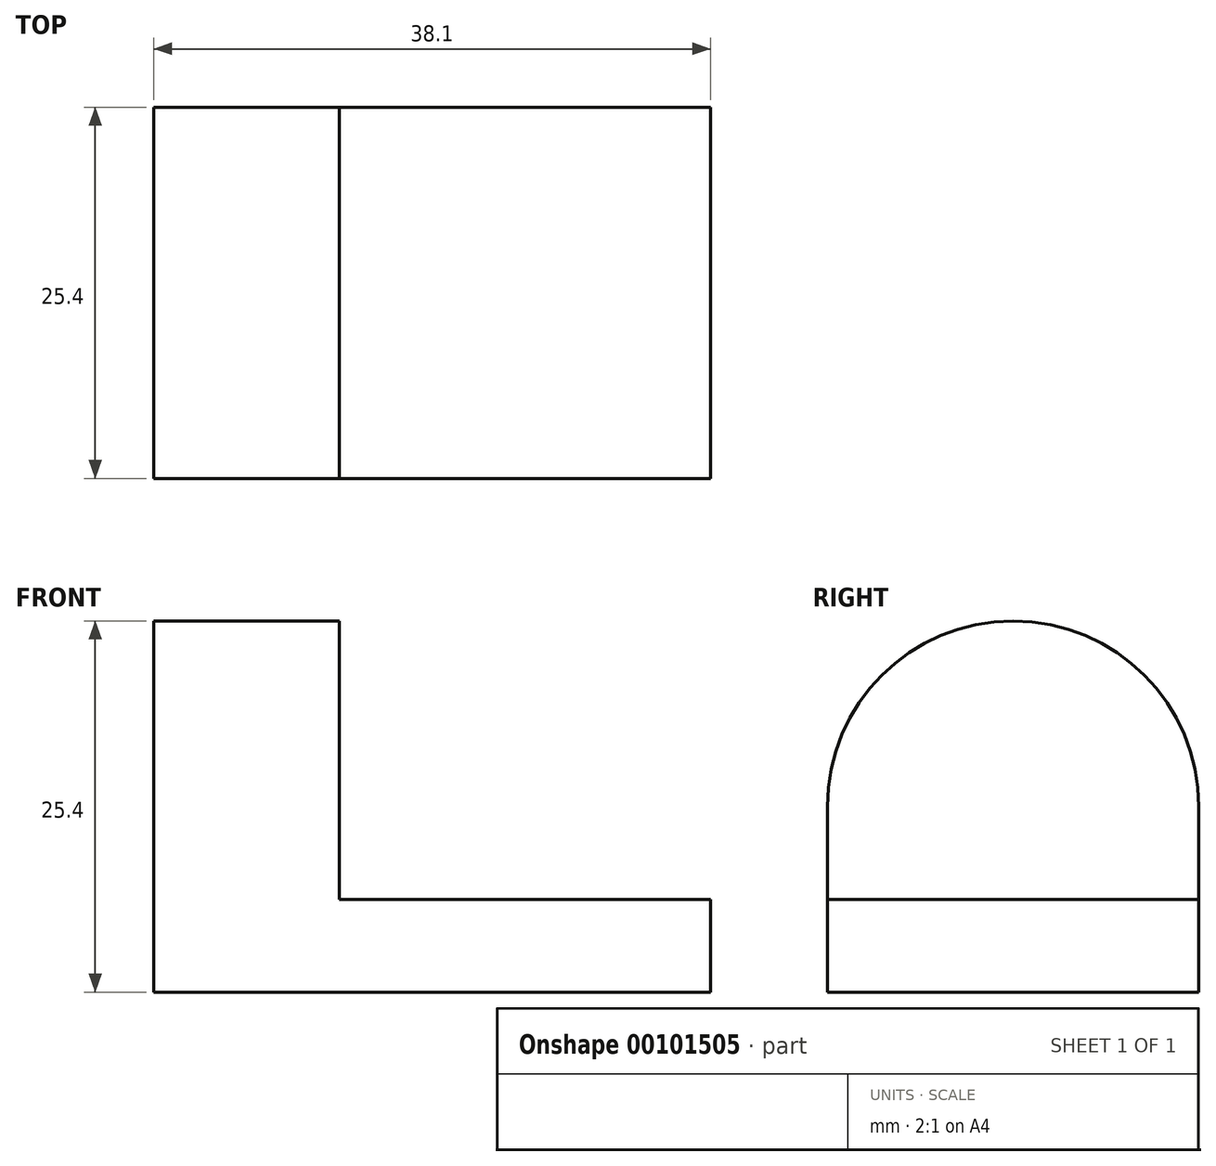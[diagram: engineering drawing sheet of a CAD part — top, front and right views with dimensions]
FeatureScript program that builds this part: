
annotation { "Feature Type Name" : "Feature", "Feature Type Description" : "" }
export const myFeature = defineFeature(function(context is Context, id is Id, definition is map)
    precondition{}
    {
        {
            var Q0;
            Q0=qCreatedBy(makeId("Front.planeOp"),FACE);
            var sketch = newSketch(context, id + "F0", { "sketchPlane" : qUnion([Q0])});
            skLineSegment(sketch, "E0.bottom", {"start": v(0, 0) * mm, "end": v(38.1, 0) * mm});
            skLineSegment(sketch, "E0.top", {"start": v(0, 6.35) * mm, "end": v(38.1, 6.35) * mm});
            skLineSegment(sketch, "E0.left", {"start": v(0, 0) * mm, "end": v(0, 6.35) * mm});
            skLineSegment(sketch, "E0.right", {"start": v(38.1, 0) * mm, "end": v(38.1, 6.35) * mm});
            skSolve(sketch);
        }
        {
            var Q0;
            Q0 = qSketchRegion(id + "F0", true);
            extrude(context, id + "F1", {"entities" : qUnion([Q0]), "endBound" : BoundingType.SYMMETRIC, "depth" : 25.4 * mm});
        }
        {
            var Q0;
            Q0=qCreatedBy(makeId("Front.planeOp"),FACE);
            var sketch = newSketch(context, id + "F2", { "sketchPlane" : qUnion([Q0])});
            skLineSegment(sketch, "E1.bottom", {"start": v(0, 6.35) * mm, "end": v(12.7, 6.35) * mm});
            skLineSegment(sketch, "E1.top", {"start": v(0, 12.7) * mm, "end": v(12.7, 12.7) * mm});
            skLineSegment(sketch, "E1.left", {"start": v(0, 6.35) * mm, "end": v(0, 12.7) * mm});
            skLineSegment(sketch, "E1.right", {"start": v(12.7, 6.35) * mm, "end": v(12.7, 12.7) * mm});
            skSolve(sketch);
        }
        {
            var Q0;
            Q0 = qSketchRegion(id + "F2", true);
            extrude(context, id + "F3", {"entities" : qUnion([Q0]), "operationType" : NewBodyOperationType.ADD, "endBound" : BoundingType.SYMMETRIC, "depth" : 25.4 * mm});
        }
        {
            var Q0;
            Q0=qCreatedBy(makeId("Right.planeOp"),FACE);
            var sketch = newSketch(context, id + "F4", { "sketchPlane" : qUnion([Q0])});
            skArc(sketch, "E2", {"start": v(12.7, 12.7) * mm, "mid": v(0, 25.4) * mm, "end": v(-12.7, 12.7) * mm});
            skLineSegment(sketch, "E3", {"start": v(-12.7, 12.7) * mm, "end": v(12.7, 12.7) * mm});
            skSolve(sketch);
        }
        {
            var Q0;
            Q0 = qSketchRegion(id + "F4", true);
            extrude(context, id + "F5", {"entities" : qUnion([Q0]), "operationType" : NewBodyOperationType.ADD, "depth" : 12.7 * mm});
        }
    });
